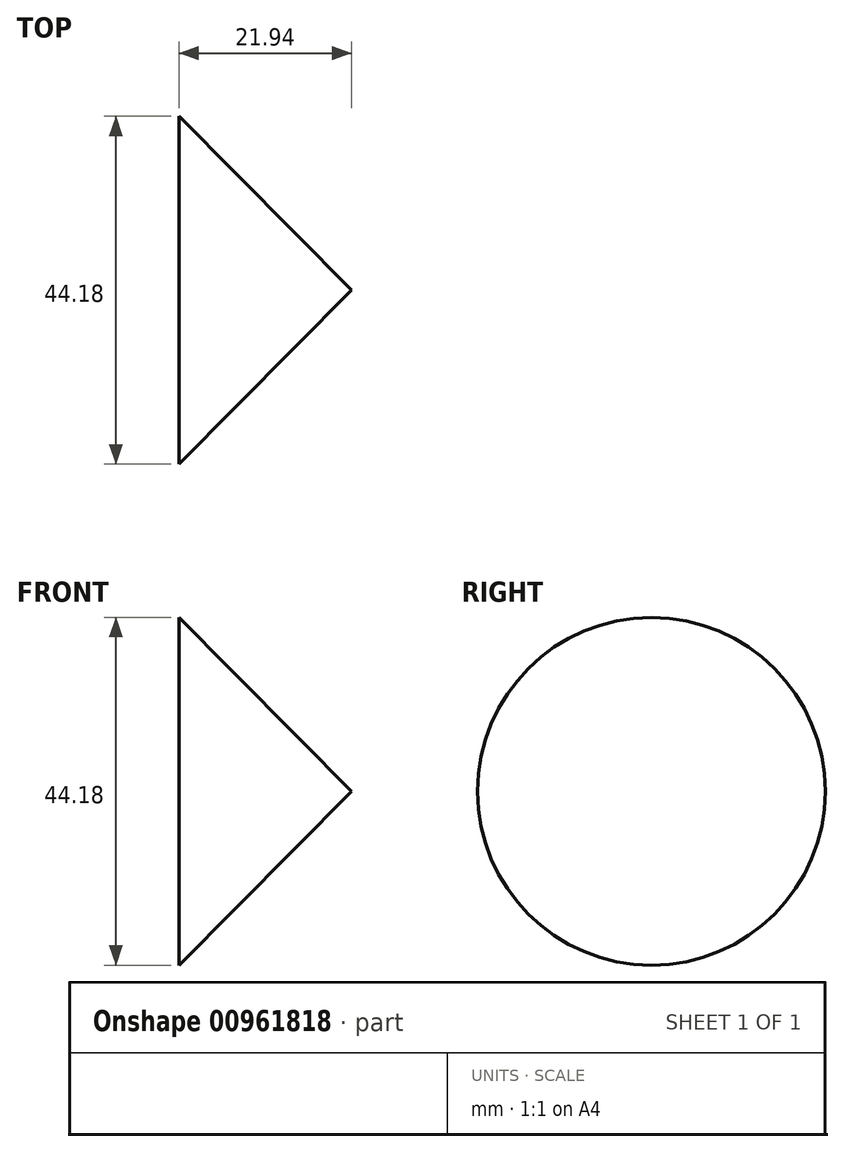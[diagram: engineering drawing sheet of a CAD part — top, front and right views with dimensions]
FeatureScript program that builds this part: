
annotation { "Feature Type Name" : "Feature", "Feature Type Description" : "" }
export const myFeature = defineFeature(function(context is Context, id is Id, definition is map)
    precondition{}
    {
        {
            var Q0;
            Q0=qCreatedBy(makeId("Front.planeOp"),FACE);
            var sketch = newSketch(context, id + "F0", { "sketchPlane" : qUnion([Q0])});
            skLineSegment(sketch, "E0", {"start": v(0, 0) * mm, "end": v(0, 22.1) * mm});
            skLineSegment(sketch, "E1", {"start": v(0, 22.1) * mm, "end": v(21.94, 0) * mm});
            skLineSegment(sketch, "E2", {"start": v(21.94, 0) * mm, "end": v(0, 0) * mm});
            skSolve(sketch);
        }
        {
            var Q0;
            Q0 = qSketchRegion(id + "F0", true);
            var Q1;
            Q1=sQuery(id+"F0.wireOp",EDGE,"E2");
            revolve(context, id + "F1", {"surfaceOperationType" : NewSurfaceOperationType.NEW, "entities" : qUnion([Q0]), "axis" : qUnion([Q1]), "revolveType" : RevolveType.FULL});
        }
    });
